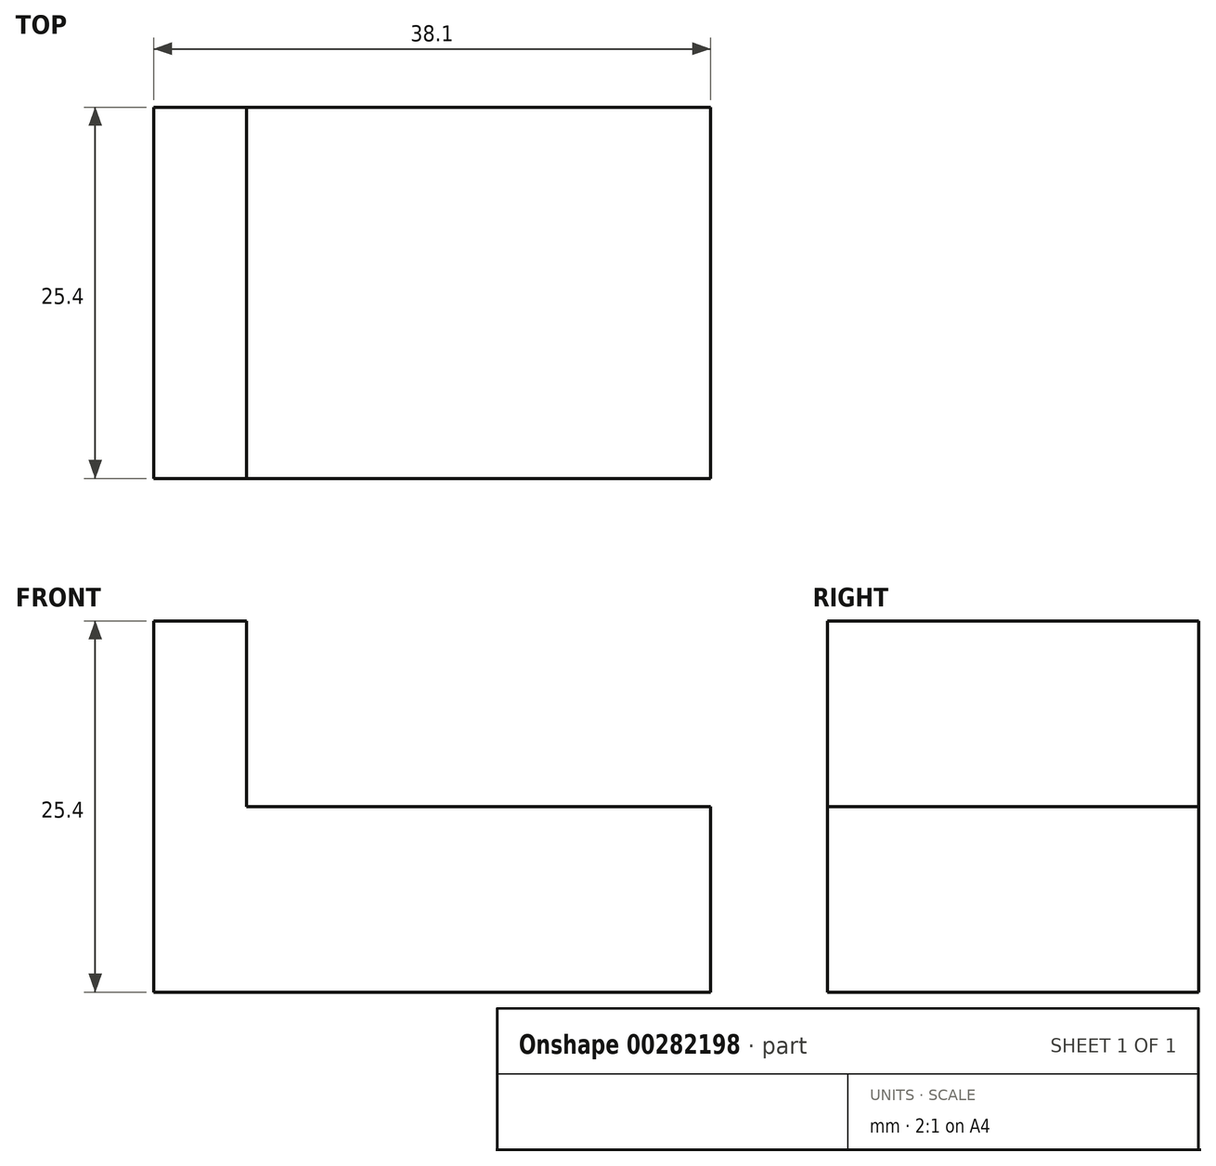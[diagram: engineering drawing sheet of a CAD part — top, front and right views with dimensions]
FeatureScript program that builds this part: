
annotation { "Feature Type Name" : "Feature", "Feature Type Description" : "" }
export const myFeature = defineFeature(function(context is Context, id is Id, definition is map)
    precondition{}
    {
        {
            var Q0;
            Q0=qCreatedBy(makeId("Front.planeOp"),FACE);
            var sketch = newSketch(context, id + "F0", { "sketchPlane" : qUnion([Q0])});
            skLineSegment(sketch, "E0.bottom", {"start": v(0, 0) * mm, "end": v(38.1, 0) * mm});
            skLineSegment(sketch, "E0.top", {"start": v(0, 12.7) * mm, "end": v(38.1, 12.7) * mm});
            skLineSegment(sketch, "E0.left", {"start": v(0, 0) * mm, "end": v(0, 12.7) * mm});
            skLineSegment(sketch, "E0.right", {"start": v(38.1, 0) * mm, "end": v(38.1, 12.7) * mm});
            skLineSegment(sketch, "E1.bottom", {"start": v(0, 12.7) * mm, "end": v(6.35, 12.7) * mm});
            skLineSegment(sketch, "E1.top", {"start": v(0, 25.4) * mm, "end": v(6.35, 25.4) * mm});
            skLineSegment(sketch, "E1.left", {"start": v(0, 12.7) * mm, "end": v(0, 25.4) * mm});
            skLineSegment(sketch, "E1.right", {"start": v(6.35, 12.7) * mm, "end": v(6.35, 25.4) * mm});
            skSolve(sketch);
        }
        {
            var Q0;
            Q0 = qSketchRegion(id + "F0", true);
            extrude(context, id + "F1", {"entities" : qUnion([Q0]), "depth" : 25.4 * mm});
        }
    });
